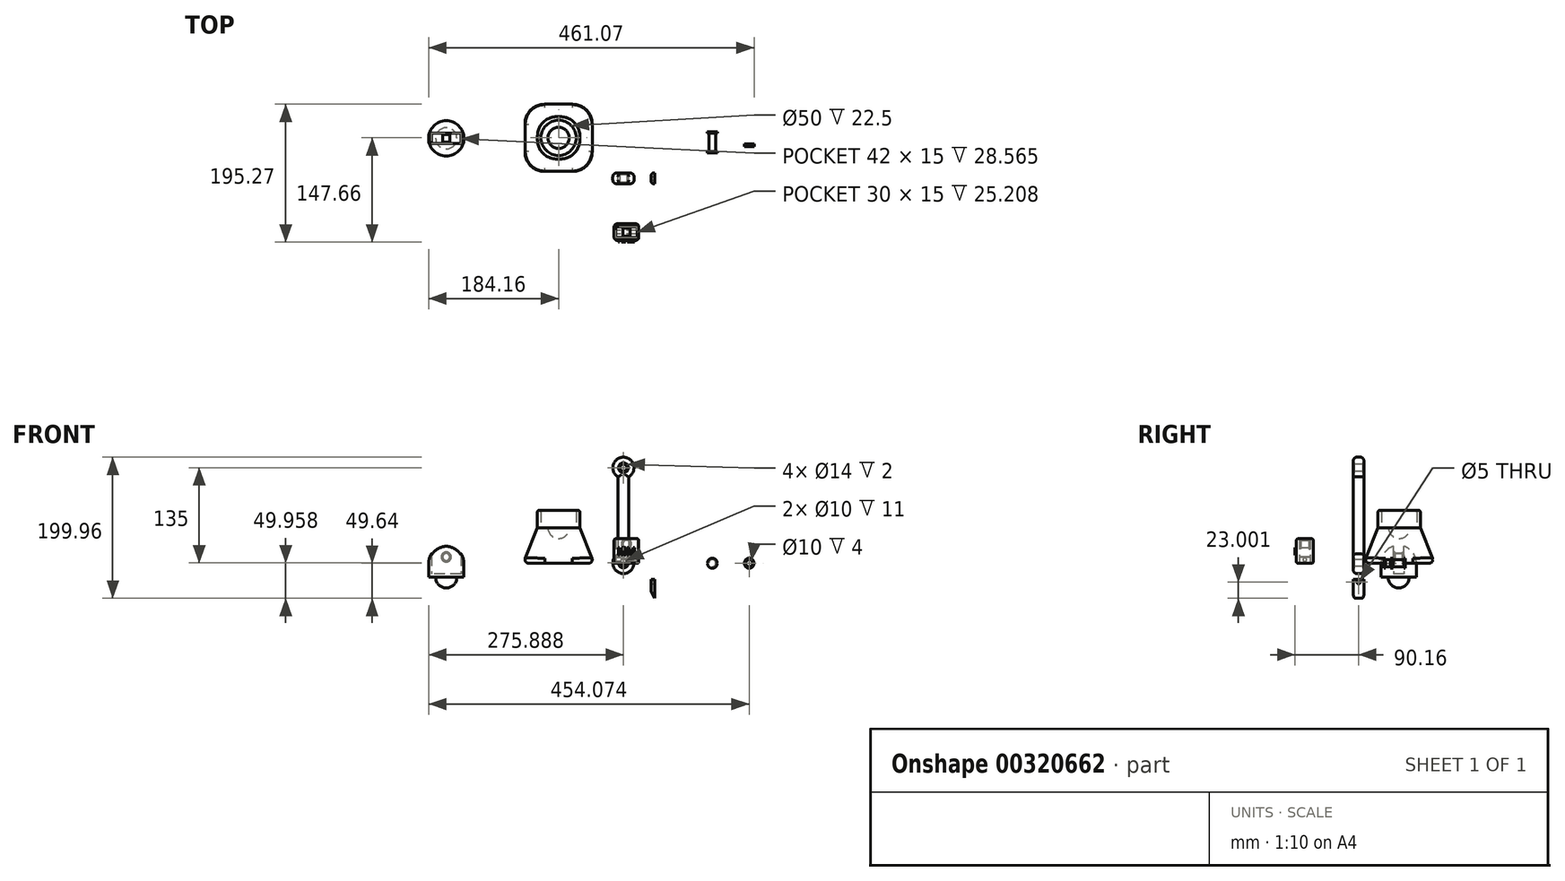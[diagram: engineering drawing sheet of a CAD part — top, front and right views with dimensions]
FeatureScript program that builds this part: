
annotation { "Feature Type Name" : "Feature", "Feature Type Description" : "" }
export const myFeature = defineFeature(function(context is Context, id is Id, definition is map)
    precondition{}
    {
        {
            var Q0;
            Q0=qCreatedBy(makeId("Top.planeOp"),FACE);
            var sketch = newSketch(context, id + "F0", { "sketchPlane" : qUnion([Q0])});
            skLineSegment(sketch, "E0.bottom", {"start": v(0, 0) * mm, "end": v(100, 0) * mm});
            skLineSegment(sketch, "E0.top", {"start": v(0, 100) * mm, "end": v(100, 100) * mm});
            skLineSegment(sketch, "E0.left", {"start": v(0, 0) * mm, "end": v(0, 100) * mm});
            skLineSegment(sketch, "E0.right", {"start": v(100, 0) * mm, "end": v(100, 100) * mm});
            skSolve(sketch);
        }
        {
            var Q0;
            Q0=makeQuery(id+"F0.imprint","IMPRINT",FACE,{"disambiguationData":[TD([[makeQuery(id+"F0.imprint","IMPRINT",EDGE,{"derivedFrom":sQuery(id+"F0.wireOp",EDGE,"E0.bottom")}),1.0]])]});
            cPlane(context, id + "F1", {"entities" : qUnion([Q0]), "cplaneType" : CPlaneType.OFFSET, "offset" : 50 * mm, "width" : 150 * mm, "height" : 150 * mm});
        }
        {
            var Q0;
            Q0=qCreatedBy(id+"F1.planeOp",FACE);
            var sketch = newSketch(context, id + "F2", { "sketchPlane" : qUnion([Q0])});
            skLineSegment(sketch, "E1.bottom", {"start": v(20, 80) * mm, "end": v(80, 80) * mm});
            skLineSegment(sketch, "E1.top", {"start": v(20, 20) * mm, "end": v(80, 20) * mm});
            skLineSegment(sketch, "E1.left", {"start": v(20, 80) * mm, "end": v(20, 20) * mm});
            skLineSegment(sketch, "E1.right", {"start": v(80, 80) * mm, "end": v(80, 20) * mm});
            skSolve(sketch);
        }
        {
            var Q0;
            Q0=makeQuery(id+"F0.imprint","IMPRINT",FACE,{"disambiguationData":[TD([[makeQuery(id+"F0.imprint","IMPRINT",EDGE,{"derivedFrom":sQuery(id+"F0.wireOp",EDGE,"E0.bottom")}),1.0]])]});
            var Q1;
            Q1=makeQuery(id+"F2.imprint","IMPRINT",FACE,{"disambiguationData":[TD([[makeQuery(id+"F2.imprint","IMPRINT",EDGE,{"derivedFrom":sQuery(id+"F2.wireOp",EDGE,"E1.bottom")}),-1.0]])]});
            loft(context, id + "F3", {"sheetProfilesArray" : [{ "sheetProfileEntities" : qUnion([Q0]) }, { "sheetProfileEntities" : qUnion([Q1]) }]});
        }
        {
            var Q0;
            Q0=makeQuery(id+"F3.opLoft","CAP_FACE",FACE,{"disambiguationData":[OSD([makeQuery(id+"F2.imprint","IMPRINT",FACE,{"disambiguationData":[TD([[makeQuery(id+"F2.imprint","IMPRINT",EDGE,{"derivedFrom":sQuery(id+"F2.wireOp",EDGE,"E1.bottom")}),-1.0]])]})])],"isStart":true});
            var sketch = newSketch(context, id + "F4", { "sketchPlane" : qUnion([Q0])});
            skLineSegment(sketch, "E2", {"start": v(50, 65) * mm, "end": v(50, 35) * mm});
            skArc(sketch, "E3", {"start": v(50, 35) * mm, "mid": v(65, 50) * mm, "end": v(50, 65) * mm});
            skPoint(sketch, "E4.orphan", {"position": v(50, 80) * mm});
            skPoint(sketch, "E5.orphan", {"position": v(50, 20) * mm});
            skSolve(sketch);
        }
        {
            var Q0;
            Q0=makeQuery(id+"F4.imprint","IMPRINT",FACE,{"disambiguationData":[TD([[makeQuery(id+"F4.imprint","IMPRINT",EDGE,{"derivedFrom":sQuery(id+"F4.wireOp",EDGE,"E2")}),1.0]])]});
            var Q1;
            Q1=sQuery(id+"F4.wireOp",EDGE,"E2");
            revolve(context, id + "F5", {"operationType" : NewBodyOperationType.REMOVE, "entities" : qUnion([Q0]), "axis" : qUnion([Q1]), "revolveType" : RevolveType.FULL, "oppositeDirection" : true});
        }
        {
            var Q0;
            Q0=makeQuery(id+"F3.opLoft","CAP_FACE",FACE,{"disambiguationData":[OSD([makeQuery(id+"F0.imprint","IMPRINT",FACE,{"disambiguationData":[TD([[makeQuery(id+"F0.imprint","IMPRINT",EDGE,{"derivedFrom":sQuery(id+"F0.wireOp",EDGE,"E0.bottom")}),1.0]])]})])],"isStart":true});
            fillet(context, id + "F6", {"entities" : qUnion([Q0]), "radius" : 5 * mm, "tangentPropagation" : true, "allowEdgeOverflow" : false});
        }
        {
            var Q0;
            Q0=makeQuery(id+"F3.opLoft","SWEPT_EDGE",EDGE,{"disambiguationData":[OSD([sQuery(id+"F0.wireOp",EDGE,"E0.bottom"),sQuery(id+"F0.wireOp",EDGE,"E0.right"),sQuery(id+"F2.wireOp",EDGE,"E1.top"),sQuery(id+"F2.wireOp",EDGE,"E1.right")])]});
            var Q1;
            Q1=makeQuery(id+"F3.opLoft","SWEPT_EDGE",EDGE,{"disambiguationData":[OSD([sQuery(id+"F0.wireOp",EDGE,"E0.top"),sQuery(id+"F0.wireOp",EDGE,"E0.right"),sQuery(id+"F2.wireOp",EDGE,"E1.bottom"),sQuery(id+"F2.wireOp",EDGE,"E1.right")])]});
            var Q2;
            Q2=makeQuery(id+"F3.opLoft","SWEPT_EDGE",EDGE,{"disambiguationData":[OSD([sQuery(id+"F0.wireOp",EDGE,"E0.top"),sQuery(id+"F0.wireOp",EDGE,"E0.left"),sQuery(id+"F2.wireOp",EDGE,"E1.bottom"),sQuery(id+"F2.wireOp",EDGE,"E1.left")])]});
            var Q3;
            Q3=makeQuery(id+"F3.opLoft","SWEPT_EDGE",EDGE,{"disambiguationData":[OSD([sQuery(id+"F0.wireOp",EDGE,"E0.bottom"),sQuery(id+"F0.wireOp",EDGE,"E0.left"),sQuery(id+"F2.wireOp",EDGE,"E1.top"),sQuery(id+"F2.wireOp",EDGE,"E1.left")])]});
            fillet(context, id + "F7", {"entities" : qUnion([Q0, Q1, Q2, Q3]), "radius" : 30 * mm, "tangentPropagation" : true, "allowEdgeOverflow" : false});
        }
        {
            var Q0;
            Q0=qCreatedBy(makeId("Top.planeOp"),FACE);
            var sketch = newSketch(context, id + "F8", { "sketchPlane" : qUnion([Q0])});
            skArc(sketch, "E6", {"start": v(184.89, 22.61) * mm, "mid": v(199.89, 37.61) * mm, "end": v(184.89, 52.61) * mm});
            skLineSegment(sketch, "E7", {"start": v(184.89, 22.61) * mm, "end": v(184.89, 52.61) * mm});
            skSolve(sketch);
        }
        {
            var Q0;
            Q0=qCreatedBy(makeId("Top.planeOp"),FACE);
            cPlane(context, id + "F9", {"entities" : qUnion([Q0]), "cplaneType" : CPlaneType.OFFSET, "offset" : 10 * mm, "width" : 150 * mm, "height" : 150 * mm});
        }
        {
            var Q0;
            Q0=qCreatedBy(id+"F9.planeOp",FACE);
            var sketch = newSketch(context, id + "F10", { "sketchPlane" : qUnion([Q0])});
            skLineSegment(sketch, "E8.bottom", {"start": v(177.39, 45.11) * mm, "end": v(192.39, 45.11) * mm});
            skLineSegment(sketch, "E8.top", {"start": v(177.39, 30.11) * mm, "end": v(192.39, 30.11) * mm});
            skLineSegment(sketch, "E8.left", {"start": v(177.39, 45.11) * mm, "end": v(177.39, 30.11) * mm});
            skLineSegment(sketch, "E8.right", {"start": v(192.39, 45.11) * mm, "end": v(192.39, 30.11) * mm});
            skSolve(sketch);
        }
        {
            var Q0;
            Q0=makeQuery(id+"F8.imprint","IMPRINT",FACE,{"disambiguationData":[TD([[makeQuery(id+"F8.imprint","IMPRINT",EDGE,{"derivedFrom":sQuery(id+"F8.wireOp",EDGE,"E6")}),1.0]])]});
            var Q1;
            Q1=sQuery(id+"F8.wireOp",EDGE,"E7");
            revolve(context, id + "F11", {"entities" : qUnion([Q0]), "axis" : qUnion([Q1]), "revolveType" : RevolveType.FULL});
        }
        {
            var Q0;
            Q0 = qSketchRegion(id + "F10", true);
            extrude(context, id + "F12", {"entities" : qUnion([Q0]), "operationType" : NewBodyOperationType.ADD, "depth" : 120 * mm});
        }
        {
            var Q0;
            Q0=makeQuery(id+"F12.boolean.opBoolean","INTERSECT",EDGE,{"derivedFrom":[makeQuery(id+"F11.opRevolve","SWEPT_FACE",FACE,{"disambiguationData":[OSD([sQuery(id+"F8.wireOp",EDGE,"E6")])]}),makeQuery(id+"F12.opExtrude","SWEPT_FACE",FACE,{"disambiguationData":[OSD([sQuery(id+"F10.wireOp",EDGE,"E8.right")])]})]});
            var Q1;
            Q1=makeQuery(id+"F12.boolean.opBoolean","INTERSECT",EDGE,{"derivedFrom":[makeQuery(id+"F11.opRevolve","SWEPT_FACE",FACE,{"disambiguationData":[OSD([sQuery(id+"F8.wireOp",EDGE,"E6")])]}),makeQuery(id+"F12.opExtrude","SWEPT_FACE",FACE,{"disambiguationData":[OSD([sQuery(id+"F10.wireOp",EDGE,"E8.top")])]})]});
            var Q2;
            Q2=makeQuery(id+"F12.boolean.opBoolean","INTERSECT",EDGE,{"derivedFrom":[makeQuery(id+"F11.opRevolve","SWEPT_FACE",FACE,{"disambiguationData":[OSD([sQuery(id+"F8.wireOp",EDGE,"E6")])]}),makeQuery(id+"F12.opExtrude","SWEPT_FACE",FACE,{"disambiguationData":[OSD([sQuery(id+"F10.wireOp",EDGE,"E8.bottom")])]})]});
            var Q3;
            Q3=makeQuery(id+"F12.boolean.opBoolean","INTERSECT",EDGE,{"derivedFrom":[makeQuery(id+"F11.opRevolve","SWEPT_FACE",FACE,{"disambiguationData":[OSD([sQuery(id+"F8.wireOp",EDGE,"E6")])]}),makeQuery(id+"F12.opExtrude","SWEPT_FACE",FACE,{"disambiguationData":[OSD([sQuery(id+"F10.wireOp",EDGE,"E8.left")])]})]});
            var Q4;
            Q4=makeQuery(id+"F12.opExtrude","SWEPT_EDGE",EDGE,{"disambiguationData":[OSD([sQuery(id+"F10.wireOp",EDGE,"E8.bottom"),sQuery(id+"F10.wireOp",EDGE,"E8.left")])]});
            var Q5;
            Q5=makeQuery(id+"F12.opExtrude","SWEPT_EDGE",EDGE,{"disambiguationData":[OSD([sQuery(id+"F10.wireOp",EDGE,"E8.bottom"),sQuery(id+"F10.wireOp",EDGE,"E8.right")])]});
            var Q6;
            Q6=makeQuery(id+"F12.opExtrude","SWEPT_EDGE",EDGE,{"disambiguationData":[OSD([sQuery(id+"F10.wireOp",EDGE,"E8.top"),sQuery(id+"F10.wireOp",EDGE,"E8.right")])]});
            var Q7;
            Q7=makeQuery(id+"F12.opExtrude","SWEPT_EDGE",EDGE,{"disambiguationData":[OSD([sQuery(id+"F10.wireOp",EDGE,"E8.top"),sQuery(id+"F10.wireOp",EDGE,"E8.left")])]});
            fillet(context, id + "F13", {"entities" : qUnion([Q0, Q1, Q2, Q3, Q4, Q5, Q6, Q7]), "radius" : 5 * mm, "tangentPropagation" : true, "allowEdgeOverflow" : false});
        }
        {
            var Q0;
            Q0=makeQuery(id+"F12.opExtrude","CAP_EDGE",EDGE,{"disambiguationData":[OSD([sQuery(id+"F10.wireOp",EDGE,"E8.right")])],"isStart":false});
            cPoint(context, id + "F14", {"entities" : qUnion([Q0]), "parameter" : 0.5});
        }
        {
            var Q0;
            Q0=makeQuery(id+"F12.opExtrude","CAP_EDGE",EDGE,{"disambiguationData":[OSD([sQuery(id+"F10.wireOp",EDGE,"E8.left")])],"isStart":false});
            cPoint(context, id + "F15", {"entities" : qUnion([Q0]), "parameter" : 0.5});
        }
        {
            var Q0;
            {var subQ0=makeQuery(id+"F12.opExtrude","SWEPT_FACE",FACE,{"disambiguationData":[OSD([sQuery(id+"F10.wireOp",EDGE,"E8.left")])]});Q0=makeQuery(id+"F13.opFillet","BLEND_EDGE",EDGE,{"blendedFrom":[makeQuery(id+"F12.boolean.opBoolean","INTERSECT",EDGE,{"derivedFrom":[makeQuery(id+"F11.opRevolve","SWEPT_FACE",FACE,{"disambiguationData":[OSD([sQuery(id+"F8.wireOp",EDGE,"E6")])]}),subQ0]}),subQ0],"blendedInto":[subQ0]});}
            cPoint(context, id + "F16", {"entities" : qUnion([Q0]), "parameter" : 0.5});
        }
        {
            var Q0;
            Q0 = qCreatedBy(id + "F14" ,VERTEX);
            var Q1;
            Q1 = qCreatedBy(id + "F15" ,VERTEX);
            var Q2;
            Q2 = qCreatedBy(id + "F16" ,VERTEX);
            cPlane(context, id + "F17", {"entities" : qUnion([Q0, Q1, Q2]), "cplaneType" : CPlaneType.THREE_POINT, "offset" : 25 * mm, "width" : 150 * mm, "height" : 150 * mm});
        }
        {
            var Q0;
            Q0=qCreatedBy(id+"F17.planeOp",FACE);
            var sketch = newSketch(context, id + "F18", { "sketchPlane" : qUnion([Q0])});
            skCircle(sketch, "E9", {"center": v(-184.89, 137.5) * mm, "radius": 15 * mm});
            skSolve(sketch);
        }
        {
            var Q0;
            Q0=makeQuery(id+"F18.imprint","IMPRINT",FACE,{"disambiguationData":[TD([[makeQuery(id+"F18.imprint","IMPRINT",EDGE,{"derivedFrom":sQuery(id+"F18.wireOp",EDGE,"E9")}),1.0]])]});
            extrude(context, id + "F19", {"entities" : qUnion([Q0]), "operationType" : NewBodyOperationType.ADD, "endBound" : BoundingType.SYMMETRIC, "depth" : 15 * mm});
        }
        {
            var Q0;
            Q0=makeQuery(id+"F19.opExtrude","CAP_EDGE",EDGE,{"disambiguationData":[OSD([sQuery(id+"F18.wireOp",EDGE,"E9")])],"isStart":true});
            var Q1;
            Q1=makeQuery(id+"F19.opExtrude","CAP_EDGE",EDGE,{"disambiguationData":[OSD([sQuery(id+"F18.wireOp",EDGE,"E9")])],"isStart":false});
            fillet(context, id + "F20", {"entities" : qUnion([Q0, Q1]), "radius" : 5 * mm, "tangentPropagation" : true, "allowEdgeOverflow" : false});
        }
        {
            var Q0;
            Q0=makeQuery(id+"F19.boolean.opBoolean","MERGE",FACE,{"derivedFrom":[makeQuery(id+"F12.opExtrude","SWEPT_FACE",FACE,{"disambiguationData":[OSD([sQuery(id+"F10.wireOp",EDGE,"E8.top")])]}),makeQuery(id+"F19.opExtrude","CAP_FACE",FACE,{"disambiguationData":[OSD([sQuery(id+"F18.wireOp",EDGE,"E9")])],"isStart":true})]});
            var sketch = newSketch(context, id + "F21", { "sketchPlane" : qUnion([Q0])});
            skCircle(sketch, "E10", {"center": v(184.89, 137.5) * mm, "radius": 5 * mm});
            skCircle(sketch, "E11", {"center": v(184.89, 137.5) * mm, "radius": 7 * mm});
            skSolve(sketch);
        }
        {
            var Q0;
            Q0=sQuery(id+"F21.wireOp",VERTEX,"E10.center");
            var Q1;
            Q1=makeQuery(id+"F11.opRevolve","SWEPT_BODY",BODY,{"disambiguationData":[OSD([sQuery(id+"F8.wireOp",EDGE,"E6"),sQuery(id+"F8.wireOp",EDGE,"E7")])]});
            hole(context, id + "F22", {"style" : HoleStyle.SIMPLE, "endStyle" : HoleEndStyle.THROUGH, "holeDiameter" : 10 * mm, "tappedDepth" : 12 * mm, "tapClearance" : 3, "locations" : qUnion([Q0]), "scope" : qUnion([Q1])});
        }
        {
            var Q0;
            Q0=makeQuery(id+"F19.boolean.opBoolean","MERGE",FACE,{"derivedFrom":[makeQuery(id+"F12.opExtrude","SWEPT_FACE",FACE,{"disambiguationData":[OSD([sQuery(id+"F10.wireOp",EDGE,"E8.bottom")])]}),makeQuery(id+"F19.opExtrude","CAP_FACE",FACE,{"disambiguationData":[OSD([sQuery(id+"F18.wireOp",EDGE,"E9")])],"isStart":false})]});
            var sketch = newSketch(context, id + "F23", { "sketchPlane" : qUnion([Q0])});
            skCircle(sketch, "E12", {"center": v(-184.89, 137.5) * mm, "radius": 7 * mm});
            skSolve(sketch);
        }
        {
            var Q0;
            Q0 = qSketchRegion(id + "F21", true);
            var Q1;
            Q1 = qSketchRegion(id + "F23", true);
            extrude(context, id + "F24", {"entities" : qUnion([Q0, Q1]), "operationType" : NewBodyOperationType.REMOVE, "oppositeDirection" : true, "depth" : 2 * mm, "hasSecondDirection" : true, "secondDirectionOppositeDirection" : false, "secondDirectionDepth" : 2 * mm});
        }
        {
            var Q0;
            Q0=qCreatedBy(makeId("Top.planeOp"),FACE);
            var sketch = newSketch(context, id + "F25", { "sketchPlane" : qUnion([Q0])});
            skLineSegment(sketch, "E13.bottom", {"start": v(267.71, 58.7) * mm, "end": v(272.71, 58.7) * mm});
            skLineSegment(sketch, "E13.top", {"start": v(267.71, 28.7) * mm, "end": v(272.71, 28.7) * mm});
            skLineSegment(sketch, "E13.left", {"start": v(267.71, 58.7) * mm, "end": v(267.71, 28.7) * mm});
            skLineSegment(sketch, "E13.right", {"start": v(272.71, 56.7) * mm, "end": v(272.71, 30.7) * mm});
            skLineSegment(sketch, "E14.bottom", {"start": v(272.71, 58.7) * mm, "end": v(274.71, 58.7) * mm});
            skLineSegment(sketch, "E14.top", {"start": v(272.71, 56.7) * mm, "end": v(274.71, 56.7) * mm});
            skLineSegment(sketch, "E14.right", {"start": v(274.71, 58.7) * mm, "end": v(274.71, 56.7) * mm});
            skLineSegment(sketch, "E15.bottom", {"start": v(272.71, 28.7) * mm, "end": v(274.71, 28.7) * mm});
            skLineSegment(sketch, "E15.top", {"start": v(272.71, 30.7) * mm, "end": v(274.71, 30.7) * mm});
            skLineSegment(sketch, "E15.right", {"start": v(274.71, 28.7) * mm, "end": v(274.71, 30.7) * mm});
            skSolve(sketch);
        }
        {
            var Q0;
            Q0=makeQuery(id+"F25.imprint","IMPRINT",FACE,{"disambiguationData":[TD([[makeQuery(id+"F25.imprint","IMPRINT",EDGE,{"derivedFrom":sQuery(id+"F25.wireOp",EDGE,"E13.bottom")}),-1.0]])]});
            var Q1;
            Q1=sQuery(id+"F25.wireOp",EDGE,"E13.left");
            revolve(context, id + "F26", {"entities" : qUnion([Q0]), "axis" : qUnion([Q1]), "revolveType" : RevolveType.FULL});
        }
        {
            var Q0;
            Q0=qCreatedBy(id+"F17.planeOp",FACE);
            var sketch = newSketch(context, id + "F27", { "sketchPlane" : qUnion([Q0])});
            skCircle(sketch, "E16", {"center": v(-319.91, 0) * mm, "radius": 7 * mm});
            skCircle(sketch, "E17", {"center": v(-319.91, 0) * mm, "radius": 5 * mm});
            skSolve(sketch);
        }
        {
            var Q0;
            Q0 = qSketchRegion(id + "F27", true);
            extrude(context, id + "F28", {"entities" : qUnion([Q0]), "depth" : 4 * mm});
        }
        {
            var Q0;
            Q0=qCreatedBy(makeId("Top.planeOp"),FACE);
            var sketch = newSketch(context, id + "F29", { "sketchPlane" : qUnion([Q0])});
            skArc(sketch, "E18", {"start": v(-109.16, 24.23) * mm, "mid": v(-84.16, 49.23) * mm, "end": v(-109.16, 74.23) * mm});
            skLineSegment(sketch, "E19", {"start": v(-109.16, 74.23) * mm, "end": v(-109.16, 24.23) * mm});
            skSolve(sketch);
        }
        {
            var Q0;
            Q0=makeQuery(id+"F29.imprint","IMPRINT",FACE,{"disambiguationData":[TD([[makeQuery(id+"F29.imprint","IMPRINT",EDGE,{"derivedFrom":sQuery(id+"F29.wireOp",EDGE,"E18")}),1.0]])]});
            var Q1;
            Q1=sQuery(id+"F29.wireOp",EDGE,"E19");
            revolve(context, id + "F30", {"entities" : qUnion([Q0]), "axis" : qUnion([Q1]), "revolveType" : RevolveType.ONE_DIRECTION, "angle" : 180 * degree});
        }
        {
            var Q0;
            Q0=qCreatedBy(makeId("Front.planeOp"),FACE);
            var sketch = newSketch(context, id + "F31", { "sketchPlane" : qUnion([Q0])});
            skLineSegment(sketch, "E20.left", {"start": v(134.23, 122.33) * mm, "end": v(134.23, 13.3) * mm});
            skLineSegment(sketch, "E20.right", {"start": v(149.23, 122.33) * mm, "end": v(149.23, 13.3) * mm});
            skArc(sketch, "E21", {"start": v(149.23, 122.33) * mm, "mid": v(141.73, 150.32) * mm, "end": v(134.23, 122.33) * mm});
            skArc(sketch, "E22", {"start": v(134.23, 13.3) * mm, "mid": v(141.73, -14.68) * mm, "end": v(149.23, 13.3) * mm});
            skSolve(sketch);
        }
        {
            var Q0;
            Q0=makeQuery(id+"F31.imprint","IMPRINT",FACE,{"disambiguationData":[TD([[makeQuery(id+"F31.imprint","IMPRINT",EDGE,{"derivedFrom":sQuery(id+"F31.wireOp",EDGE,"E20.left")}),1.0]])]});
            extrude(context, id + "F32", {"entities" : qUnion([Q0]), "depth" : 15 * mm});
        }
        {
            var Q0;
            Q0=makeQuery(id+"F32.opExtrude","CAP_FACE",FACE,{"disambiguationData":[OSD([sQuery(id+"F31.wireOp",EDGE,"E20.left"),sQuery(id+"F31.wireOp",EDGE,"E20.right"),sQuery(id+"F31.wireOp",EDGE,"E21"),sQuery(id+"F31.wireOp",EDGE,"E22")])],"isStart":false});
            var Q1;
            Q1=makeQuery(id+"F32.opExtrude","CAP_FACE",FACE,{"disambiguationData":[OSD([sQuery(id+"F31.wireOp",EDGE,"E20.left"),sQuery(id+"F31.wireOp",EDGE,"E20.right"),sQuery(id+"F31.wireOp",EDGE,"E21"),sQuery(id+"F31.wireOp",EDGE,"E22")])],"isStart":true});
            fillet(context, id + "F33", {"entities" : qUnion([Q0, Q1]), "radius" : 5 * mm, "tangentPropagation" : true, "allowEdgeOverflow" : false});
        }
        {
            var Q0;
            Q0=makeQuery(id+"F32.opExtrude","CAP_FACE",FACE,{"disambiguationData":[OSD([sQuery(id+"F31.wireOp",EDGE,"E20.left"),sQuery(id+"F31.wireOp",EDGE,"E20.right"),sQuery(id+"F31.wireOp",EDGE,"E21"),sQuery(id+"F31.wireOp",EDGE,"E22")])],"isStart":false});
            var sketch = newSketch(context, id + "F34", { "sketchPlane" : qUnion([Q0])});
            skCircle(sketch, "E23", {"center": v(141.73, 135.32) * mm, "radius": 5 * mm});
            skCircle(sketch, "E24", {"center": v(141.73, 0.32) * mm, "radius": 5 * mm});
            skCircle(sketch, "E25", {"center": v(141.73, 135.32) * mm, "radius": 7 * mm});
            skCircle(sketch, "E26", {"center": v(141.73, 0.32) * mm, "radius": 7 * mm});
            skSolve(sketch);
        }
        {
            var Q0;
            Q0=makeQuery(id+"F34.imprint","IMPRINT",FACE,{"disambiguationData":[TD([[makeQuery(id+"F34.imprint","IMPRINT",EDGE,{"derivedFrom":sQuery(id+"F34.wireOp",EDGE,"E23")}),1.0]])]});
            var Q1;
            Q1=makeQuery(id+"F34.imprint","IMPRINT",FACE,{"disambiguationData":[TD([[makeQuery(id+"F34.imprint","IMPRINT",EDGE,{"derivedFrom":sQuery(id+"F34.wireOp",EDGE,"E24")}),1.0]])]});
            extrude(context, id + "F35", {"entities" : qUnion([Q0, Q1]), "operationType" : NewBodyOperationType.REMOVE, "endBound" : BoundingType.THROUGH_ALL, "oppositeDirection" : true, "depth" : 25 * mm});
        }
        {
            var Q0;
            Q0 = qSketchRegion(id + "F34", true);
            extrude(context, id + "F36", {"entities" : qUnion([Q0]), "operationType" : NewBodyOperationType.REMOVE, "oppositeDirection" : true, "depth" : 2 * mm});
        }
        {
            var Q0;
            Q0=makeQuery(id+"F32.opExtrude","CAP_FACE",FACE,{"disambiguationData":[OSD([sQuery(id+"F31.wireOp",EDGE,"E20.left"),sQuery(id+"F31.wireOp",EDGE,"E20.right"),sQuery(id+"F31.wireOp",EDGE,"E21"),sQuery(id+"F31.wireOp",EDGE,"E22")])],"isStart":true});
            var sketch = newSketch(context, id + "F37", { "sketchPlane" : qUnion([Q0])});
            skCircle(sketch, "E27", {"center": v(-141.73, 135.32) * mm, "radius": 7 * mm});
            skCircle(sketch, "E28", {"center": v(-141.73, 0.32) * mm, "radius": 7 * mm});
            skSolve(sketch);
        }
        {
            var Q0;
            Q0 = qSketchRegion(id + "F37", true);
            extrude(context, id + "F38", {"entities" : qUnion([Q0]), "operationType" : NewBodyOperationType.REMOVE, "oppositeDirection" : true, "depth" : 2 * mm});
        }
        {
            var Q0;
            Q0=makeQuery(id+"F30.opRevolve","CAP_FACE",FACE,{"disambiguationData":[OSD([sQuery(id+"F29.wireOp",EDGE,"E18"),sQuery(id+"F29.wireOp",EDGE,"E19")])],"isStart":true});
            var sketch = newSketch(context, id + "F39", { "sketchPlane" : qUnion([Q0])});
            skLineSegment(sketch, "E29.bottom", {"start": v(-88.16, -56.73) * mm, "end": v(-130.16, -56.73) * mm});
            skLineSegment(sketch, "E29.top", {"start": v(-88.16, -41.73) * mm, "end": v(-130.16, -41.73) * mm});
            skLineSegment(sketch, "E29.left", {"start": v(-88.16, -56.73) * mm, "end": v(-88.16, -41.73) * mm});
            skLineSegment(sketch, "E29.right", {"start": v(-130.16, -56.73) * mm, "end": v(-130.16, -41.73) * mm});
            skSolve(sketch);
        }
        {
            var Q0;
            Q0=makeQuery(id+"F39.imprint","IMPRINT",FACE,{"disambiguationData":[TD([[makeQuery(id+"F39.imprint","IMPRINT",EDGE,{"derivedFrom":sQuery(id+"F39.wireOp",EDGE,"E29.bottom")}),1.0]])]});
            var Q1;
            Q1=makeQuery(id+"F39.imprint","IMPRINT",FACE,{"disambiguationData":[TD([[makeQuery(id+"F39.imprint","IMPRINT",EDGE,{"derivedFrom":sQuery(id+"F39.wireOp",EDGE,"E29.bottom")}),-1.0]])]});
            extrude(context, id + "F40", {"entities" : qUnion([Q0, Q1]), "operationType" : NewBodyOperationType.ADD, "depth" : 20 * mm});
        }
        {
            var Q0;
            Q0=makeQuery(id+"F40.opExtrude","CAP_FACE",FACE,{"disambiguationData":[OSD([sQuery(id+"F29.wireOp",EDGE,"E18")])],"isStart":false});
            var sketch = newSketch(context, id + "F41", { "sketchPlane" : qUnion([Q0])});
            skArc(sketch, "E30", {"start": v(-109.16, -34.23) * mm, "mid": v(-124.16, -49.23) * mm, "end": v(-109.16, -64.23) * mm});
            skLineSegment(sketch, "E31", {"start": v(-109.16, -64.23) * mm, "end": v(-109.16, -34.23) * mm});
            skSolve(sketch);
        }
        {
            var Q0;
            Q0=makeQuery(id+"F41.imprint","IMPRINT",FACE,{"disambiguationData":[TD([[makeQuery(id+"F41.imprint","IMPRINT",EDGE,{"derivedFrom":sQuery(id+"F41.wireOp",EDGE,"E30")}),1.0]])]});
            var Q1;
            Q1=sQuery(id+"F41.wireOp",EDGE,"E31");
            revolve(context, id + "F42", {"operationType" : NewBodyOperationType.ADD, "entities" : qUnion([Q0]), "axis" : qUnion([Q1]), "revolveType" : RevolveType.FULL});
        }
        {
            var Q0;
            Q0 = qSketchRegion(id + "F39", true);
            extrude(context, id + "F43", {"entities" : qUnion([Q0]), "operationType" : NewBodyOperationType.REMOVE, "endBound" : BoundingType.THROUGH_ALL, "oppositeDirection" : true, "depth" : 25 * mm, "hasSecondDirection" : true, "secondDirectionOppositeDirection" : false, "secondDirectionDepth" : 15 * mm});
        }
        {
            var Q0;
            Q0=makeQuery(id+"F43.boolean.opBoolean","COPY",FACE,{"derivedFrom":makeQuery(id+"F43.opExtrude","SWEPT_FACE",FACE,{"disambiguationData":[OSD([sQuery(id+"F39.wireOp",EDGE,"E29.top")])]})});
            var sketch = newSketch(context, id + "F44", { "sketchPlane" : qUnion([Q0])});
            skCircle(sketch, "E32", {"center": v(109.16, 8.85) * mm, "radius": 7 * mm});
            skPoint(sketch, "E32.centerSnap0", {"position": v(109.16, 23.85) * mm});
            skPoint(sketch, "E32.centerSnap1", {"position": v(130.16, -1.85) * mm});
            skSolve(sketch);
        }
        {
            var Q0;
            Q0=makeQuery(id+"F44.imprint","IMPRINT",FACE,{"disambiguationData":[TD([[makeQuery(id+"F44.imprint","IMPRINT",EDGE,{"derivedFrom":sQuery(id+"F44.wireOp",EDGE,"E32")}),1.0]])]});
            extrude(context, id + "F45", {"entities" : qUnion([Q0]), "operationType" : NewBodyOperationType.ADD, "depth" : 2 * mm});
        }
        {
            var Q0;
            Q0=makeQuery(id+"F45.opExtrude","CAP_FACE",FACE,{"disambiguationData":[OSD([sQuery(id+"F44.wireOp",EDGE,"E32")])],"isStart":false});
            var sketch = newSketch(context, id + "F46", { "sketchPlane" : qUnion([Q0])});
            skCircle(sketch, "E33", {"center": v(109.16, 8.85) * mm, "radius": 5 * mm});
            skSolve(sketch);
        }
        {
            var Q0;
            Q0=makeQuery(id+"F46.imprint","IMPRINT",FACE,{"disambiguationData":[TD([[makeQuery(id+"F46.imprint","IMPRINT",EDGE,{"derivedFrom":sQuery(id+"F46.wireOp",EDGE,"E33")}),1.0]])]});
            extrude(context, id + "F47", {"entities" : qUnion([Q0]), "operationType" : NewBodyOperationType.ADD, "endBound" : BoundingType.UP_TO_NEXT, "depth" : 25 * mm});
        }
        {
            var Q0;
            Q0=qCreatedBy(makeId("Top.planeOp"),FACE);
            var sketch = newSketch(context, id + "F48", { "sketchPlane" : qUnion([Q0])});
            skLineSegment(sketch, "E34.bottom", {"start": v(203.21, -84.7) * mm, "end": v(208.21, -84.7) * mm});
            skLineSegment(sketch, "E34.top", {"start": v(203.21, -99.7) * mm, "end": v(208.21, -99.7) * mm});
            skLineSegment(sketch, "E34.left", {"start": v(198.21, -89.7) * mm, "end": v(198.21, -94.7) * mm});
            skLineSegment(sketch, "E34.right", {"start": v(213.21, -89.7) * mm, "end": v(213.21, -94.7) * mm});
            skPoint(sketch, "E35.visualSharp", {"position": v(198.21, -84.7) * mm});
            skArc(sketch, "E35.filletArc", {"start": v(203.21, -84.7) * mm, "mid": v(199.68, -86.16) * mm, "end": v(198.21, -89.7) * mm});
            skPoint(sketch, "E36.visualSharp", {"position": v(213.21, -84.7) * mm});
            skArc(sketch, "E36.filletArc", {"start": v(213.21, -89.7) * mm, "mid": v(211.75, -86.16) * mm, "end": v(208.21, -84.7) * mm});
            skPoint(sketch, "E37.visualSharp", {"position": v(213.21, -99.7) * mm});
            skArc(sketch, "E37.filletArc", {"start": v(208.21, -99.7) * mm, "mid": v(211.75, -98.23) * mm, "end": v(213.21, -94.7) * mm});
            skPoint(sketch, "E38.visualSharp", {"position": v(198.21, -99.7) * mm});
            skArc(sketch, "E38.filletArc", {"start": v(198.21, -94.7) * mm, "mid": v(199.68, -98.23) * mm, "end": v(203.21, -99.7) * mm});
            skLineSegment(sketch, "E39.bottom", {"start": v(192.71, -74.2) * mm, "end": v(218.71, -74.2) * mm});
            skLineSegment(sketch, "E39.top", {"start": v(192.71, -110.2) * mm, "end": v(218.71, -110.2) * mm});
            skLineSegment(sketch, "E39.left", {"start": v(187.71, -79.2) * mm, "end": v(187.71, -105.2) * mm});
            skLineSegment(sketch, "E39.right", {"start": v(223.71, -79.2) * mm, "end": v(223.71, -105.2) * mm});
            skPoint(sketch, "E40.visualSharp", {"position": v(187.71, -74.2) * mm});
            skArc(sketch, "E40.filletArc", {"start": v(192.71, -74.2) * mm, "mid": v(189.18, -75.66) * mm, "end": v(187.71, -79.2) * mm});
            skPoint(sketch, "E41.visualSharp", {"position": v(223.71, -74.2) * mm});
            skArc(sketch, "E41.filletArc", {"start": v(223.71, -79.2) * mm, "mid": v(222.25, -75.66) * mm, "end": v(218.71, -74.2) * mm});
            skPoint(sketch, "E42.visualSharp", {"position": v(223.71, -110.2) * mm});
            skArc(sketch, "E42.filletArc", {"start": v(218.71, -110.2) * mm, "mid": v(222.25, -108.73) * mm, "end": v(223.71, -105.2) * mm});
            skPoint(sketch, "E43.visualSharp", {"position": v(187.71, -110.2) * mm});
            skArc(sketch, "E43.filletArc", {"start": v(187.71, -105.2) * mm, "mid": v(189.18, -108.73) * mm, "end": v(192.71, -110.2) * mm});
            skSolve(sketch);
        }
        {
            var Q0;
            Q0=makeQuery(id+"F48.imprint","IMPRINT",FACE,{"disambiguationData":[TD([[makeQuery(id+"F48.imprint","IMPRINT",EDGE,{"derivedFrom":sQuery(id+"F48.wireOp",EDGE,"E34.bottom")}),1.0]])]});
            extrude(context, id + "F49", {"entities" : qUnion([Q0]), "depth" : 20 * mm});
        }
        {
            var Q0;
            Q0=makeQuery(id+"F49.opExtrude","CAP_EDGE",EDGE,{"disambiguationData":[OSD([sQuery(id+"F48.wireOp",EDGE,"E39.left")])],"isStart":false});
            fillet(context, id + "F50", {"entities" : qUnion([Q0]), "radius" : 10 * mm, "tangentPropagation" : true, "allowEdgeOverflow" : false});
        }
        {
            var Q0;
            Q0=makeQuery(id+"F49.opExtrude","CAP_EDGE",EDGE,{"disambiguationData":[OSD([sQuery(id+"F48.wireOp",EDGE,"E34.top")])],"isStart":true});
            var Q1;
            Q1=makeQuery(id+"F49.opExtrude","CAP_EDGE",EDGE,{"disambiguationData":[OSD([sQuery(id+"F48.wireOp",EDGE,"E37.filletArc")])],"isStart":true});
            fillet(context, id + "F51", {"entities" : qUnion([Q0, Q1]), "radius" : 5 * mm, "tangentPropagation" : true, "allowEdgeOverflow" : false});
        }
        {
            var Q0;
            Q0=makeQuery(id+"F11.opRevolve","SWEPT_BODY",BODY,{"disambiguationData":[OSD([sQuery(id+"F8.wireOp",EDGE,"E6"),sQuery(id+"F8.wireOp",EDGE,"E7")])]});
            deleteBodies(context, id + "F52", {"entities" : qUnion([Q0])});
        }
        {
            var Q0;
            Q0=makeQuery(id+"F49.opExtrude","SWEPT_BODY",BODY,{"disambiguationData":[OSD([sQuery(id+"F48.wireOp",EDGE,"E34.bottom"),sQuery(id+"F48.wireOp",EDGE,"E34.top"),sQuery(id+"F48.wireOp",EDGE,"E34.left"),sQuery(id+"F48.wireOp",EDGE,"E34.right"),sQuery(id+"F48.wireOp",EDGE,"E35.filletArc"),sQuery(id+"F48.wireOp",EDGE,"E36.filletArc"),sQuery(id+"F48.wireOp",EDGE,"E37.filletArc"),sQuery(id+"F48.wireOp",EDGE,"E38.filletArc"),sQuery(id+"F48.wireOp",EDGE,"E39.bottom"),sQuery(id+"F48.wireOp",EDGE,"E39.top"),sQuery(id+"F48.wireOp",EDGE,"E39.left"),sQuery(id+"F48.wireOp",EDGE,"E39.right"),sQuery(id+"F48.wireOp",EDGE,"E40.filletArc"),sQuery(id+"F48.wireOp",EDGE,"E41.filletArc"),sQuery(id+"F48.wireOp",EDGE,"E42.filletArc"),sQuery(id+"F48.wireOp",EDGE,"E43.filletArc")])]});
            deleteBodies(context, id + "F53", {"entities" : qUnion([Q0])});
        }
        {
            var Q0;
            Q0=makeQuery(id+"F43.boolean.opBoolean","COPY",FACE,{"derivedFrom":makeQuery(id+"F43.opExtrude","SWEPT_FACE",FACE,{"disambiguationData":[OSD([sQuery(id+"F39.wireOp",EDGE,"E29.bottom")])]})});
            var sketch = newSketch(context, id + "F54", { "sketchPlane" : qUnion([Q0])});
            skCircle(sketch, "E44", {"center": v(-109.16, 8.85) * mm, "radius": 7 * mm});
            skSolve(sketch);
        }
        {
            var Q0;
            Q0=makeQuery(id+"F54.imprint","IMPRINT",FACE,{"disambiguationData":[TD([[makeQuery(id+"F54.imprint","IMPRINT",EDGE,{"derivedFrom":sQuery(id+"F54.wireOp",EDGE,"E44")}),1.0]])]});
            extrude(context, id + "F55", {"entities" : qUnion([Q0]), "operationType" : NewBodyOperationType.ADD, "depth" : 2 * mm});
        }
        {
            var Q0;
            Q0=qCreatedBy(makeId("Top.planeOp"),FACE);
            var sketch = newSketch(context, id + "F56", { "sketchPlane" : qUnion([Q0])});
            skLineSegment(sketch, "E45.bottom", {"start": v(133.56, -71.66) * mm, "end": v(158.56, -71.66) * mm});
            skLineSegment(sketch, "E45.top", {"start": v(133.56, -95.66) * mm, "end": v(158.56, -95.66) * mm});
            skLineSegment(sketch, "E45.left", {"start": v(128.56, -76.66) * mm, "end": v(128.56, -90.66) * mm});
            skLineSegment(sketch, "E45.right", {"start": v(163.56, -76.66) * mm, "end": v(163.56, -90.66) * mm});
            skPoint(sketch, "E46.visualSharp", {"position": v(163.56, -71.66) * mm});
            skArc(sketch, "E46.filletArc", {"start": v(163.56, -76.66) * mm, "mid": v(162.1, -73.13) * mm, "end": v(158.56, -71.66) * mm});
            skPoint(sketch, "E47.visualSharp", {"position": v(163.56, -95.66) * mm});
            skArc(sketch, "E47.filletArc", {"start": v(158.56, -95.66) * mm, "mid": v(162.1, -94.2) * mm, "end": v(163.56, -90.66) * mm});
            skPoint(sketch, "E48.visualSharp", {"position": v(128.56, -95.66) * mm});
            skArc(sketch, "E48.filletArc", {"start": v(128.56, -90.66) * mm, "mid": v(130.03, -94.2) * mm, "end": v(133.56, -95.66) * mm});
            skPoint(sketch, "E49.visualSharp", {"position": v(128.56, -71.66) * mm});
            skArc(sketch, "E49.filletArc", {"start": v(133.56, -71.66) * mm, "mid": v(130.03, -73.13) * mm, "end": v(128.56, -76.66) * mm});
            skPoint(sketch, "E50.firstSnap0", {"position": v(146.06, -71.66) * mm});
            skLineSegment(sketch, "E50.bottom", {"start": v(131.06, -76.16) * mm, "end": v(161.06, -76.16) * mm});
            skLineSegment(sketch, "E50.top", {"start": v(131.06, -91.16) * mm, "end": v(161.06, -91.16) * mm});
            skLineSegment(sketch, "E50.left", {"start": v(131.06, -76.16) * mm, "end": v(131.06, -91.16) * mm});
            skLineSegment(sketch, "E50.right", {"start": v(161.06, -76.16) * mm, "end": v(161.06, -91.16) * mm});
            skSolve(sketch);
        }
        {
            var Q0;
            Q0=makeQuery(id+"F56.imprint","IMPRINT",FACE,{"disambiguationData":[TD([[makeQuery(id+"F56.imprint","IMPRINT",EDGE,{"derivedFrom":sQuery(id+"F56.wireOp",EDGE,"E45.bottom")}),-1.0]])]});
            extrude(context, id + "F57", {"entities" : qUnion([Q0]), "depth" : 35 * mm});
        }
        {
            var Q0;
            Q0=makeQuery(id+"F57.opExtrude","SWEPT_FACE",FACE,{"disambiguationData":[OSD([sQuery(id+"F56.wireOp",EDGE,"E50.bottom")])]});
            var sketch = newSketch(context, id + "F58", { "sketchPlane" : qUnion([Q0])});
            skCircle(sketch, "E51", {"center": v(146.06, 27.5) * mm, "radius": 5 * mm});
            skCircle(sketch, "E52", {"center": v(146.06, 27.5) * mm, "radius": 7 * mm});
            skSolve(sketch);
        }
        {
            var Q0;
            Q0=makeQuery(id+"F58.imprint","IMPRINT",FACE,{"disambiguationData":[TD([[makeQuery(id+"F58.imprint","IMPRINT",EDGE,{"derivedFrom":sQuery(id+"F58.wireOp",EDGE,"E51")}),1.0]])]});
            extrude(context, id + "F59", {"entities" : qUnion([Q0]), "operationType" : NewBodyOperationType.ADD, "endBound" : BoundingType.UP_TO_NEXT, "depth" : 25 * mm});
        }
        {
            var Q0;
            Q0=makeQuery(id+"F58.imprint","IMPRINT",FACE,{"disambiguationData":[TD([[makeQuery(id+"F58.imprint","IMPRINT",EDGE,{"derivedFrom":sQuery(id+"F58.wireOp",EDGE,"E51")}),-1.0]])]});
            extrude(context, id + "F60", {"entities" : qUnion([Q0]), "operationType" : NewBodyOperationType.ADD, "depth" : 2 * mm});
        }
        {
            var Q0;
            Q0=makeQuery(id+"F57.opExtrude","SWEPT_FACE",FACE,{"disambiguationData":[OSD([sQuery(id+"F56.wireOp",EDGE,"E50.top")])]});
            var sketch = newSketch(context, id + "F61", { "sketchPlane" : qUnion([Q0])});
            skCircle(sketch, "E53", {"center": v(-146.06, 27.5) * mm, "radius": 7 * mm});
            skSolve(sketch);
        }
        {
            var Q0;
            Q0=makeQuery(id+"F61.imprint","IMPRINT",FACE,{"disambiguationData":[TD([[makeQuery(id+"F61.imprint","IMPRINT",EDGE,{"derivedFrom":sQuery(id+"F61.wireOp",EDGE,"E53")}),1.0]])]});
            extrude(context, id + "F62", {"entities" : qUnion([Q0]), "operationType" : NewBodyOperationType.ADD, "depth" : 2 * mm});
        }
        {
            var Q0;
            Q0=qCreatedBy(makeId("Front.planeOp"),FACE);
            var sketch = newSketch(context, id + "F63", { "sketchPlane" : qUnion([Q0])});
            skLineSegment(sketch, "E54", {"start": v(181.27, -22.64) * mm, "end": v(181.27, -40.64) * mm});
            skLineSegment(sketch, "E55", {"start": v(181.27, -40.64) * mm, "end": v(186.27, -49.64) * mm});
            skLineSegment(sketch, "E56", {"start": v(186.27, -49.64) * mm, "end": v(186.27, -22.64) * mm});
            skLineSegment(sketch, "E57", {"start": v(186.27, -22.64) * mm, "end": v(181.27, -22.64) * mm});
            skSolve(sketch);
        }
        {
            var Q0;
            Q0=makeQuery(id+"F63.imprint","IMPRINT",FACE,{"disambiguationData":[TD([[makeQuery(id+"F63.imprint","IMPRINT",EDGE,{"derivedFrom":sQuery(id+"F63.wireOp",EDGE,"E54")}),1.0]])]});
            extrude(context, id + "F64", {"entities" : qUnion([Q0]), "depth" : 15 * mm});
        }
        {
            var Q0;
            Q0=makeQuery(id+"F57.opExtrude","SWEPT_FACE",FACE,{"disambiguationData":[OSD([sQuery(id+"F56.wireOp",EDGE,"E50.left")])]});
            var sketch = newSketch(context, id + "F65", { "sketchPlane" : qUnion([Q0])});
            skCircle(sketch, "E58", {"center": v(-83.66, 5) * mm, "radius": 2.5 * mm});
            skPoint(sketch, "E58.centerSnap0", {"position": v(-83.66, 0) * mm});
            skLineSegment(sketch, "E59.bottom", {"start": v(-91.16, 9.75) * mm, "end": v(-76.16, 9.75) * mm});
            skLineSegment(sketch, "E59.top", {"start": v(-91.16, 9) * mm, "end": v(-76.16, 9) * mm});
            skLineSegment(sketch, "E59.left", {"start": v(-91.16, 9.75) * mm, "end": v(-91.16, 9) * mm});
            skLineSegment(sketch, "E59.right", {"start": v(-76.16, 9.75) * mm, "end": v(-76.16, 9) * mm});
            skSolve(sketch);
        }
        {
            var Q0;
            Q0=makeQuery(id+"F65.imprint","IMPRINT",FACE,{"disambiguationData":[TD([[makeQuery(id+"F65.imprint","IMPRINT",EDGE,{"derivedFrom":sQuery(id+"F65.wireOp",EDGE,"E58")}),1.0]])]});
            var Q1;
            Q1=makeQuery(id+"F65.imprint","IMPRINT",FACE,{"disambiguationData":[TD([[makeQuery(id+"F65.imprint","IMPRINT",EDGE,{"derivedFrom":sQuery(id+"F65.wireOp",EDGE,"E59.bottom")}),-1.0]])]});
            extrude(context, id + "F66", {"entities" : qUnion([Q0, Q1]), "operationType" : NewBodyOperationType.ADD, "endBound" : BoundingType.UP_TO_NEXT, "depth" : 25 * mm});
        }
        {
            var Q0;
            Q0=makeQuery(id+"F64.opExtrude","SWEPT_FACE",FACE,{"disambiguationData":[OSD([sQuery(id+"F63.wireOp",EDGE,"E56")])]});
            var sketch = newSketch(context, id + "F67", { "sketchPlane" : qUnion([Q0])});
            skCircle(sketch, "E60", {"center": v(-7.5, -26.64) * mm, "radius": 2.5 * mm});
            skPoint(sketch, "E60.centerSnap0", {"position": v(-7.5, -22.64) * mm});
            skSolve(sketch);
        }
        {
            var Q0;
            Q0=makeQuery(id+"F67.imprint","IMPRINT",FACE,{"disambiguationData":[TD([[makeQuery(id+"F67.imprint","IMPRINT",EDGE,{"derivedFrom":sQuery(id+"F67.wireOp",EDGE,"E60")}),1.0]])]});
            extrude(context, id + "F68", {"entities" : qUnion([Q0]), "operationType" : NewBodyOperationType.REMOVE, "endBound" : BoundingType.UP_TO_NEXT, "oppositeDirection" : true, "depth" : 25 * mm});
        }
        {
            var Q0;
            Q0=makeQuery(id+"F57.opExtrude","CAP_EDGE",EDGE,{"disambiguationData":[OSD([sQuery(id+"F56.wireOp",EDGE,"E45.top")])],"isStart":true});
            var Q1;
            Q1=makeQuery(id+"F57.opExtrude","CAP_EDGE",EDGE,{"disambiguationData":[OSD([sQuery(id+"F56.wireOp",EDGE,"E45.right")])],"isStart":true});
            var Q2;
            Q2=makeQuery(id+"F57.opExtrude","CAP_EDGE",EDGE,{"disambiguationData":[OSD([sQuery(id+"F56.wireOp",EDGE,"E47.filletArc")])],"isStart":true});
            var Q3;
            Q3=makeQuery(id+"F57.opExtrude","CAP_EDGE",EDGE,{"disambiguationData":[OSD([sQuery(id+"F56.wireOp",EDGE,"E45.bottom")])],"isStart":true});
            var Q4;
            Q4=makeQuery(id+"F57.opExtrude","CAP_EDGE",EDGE,{"disambiguationData":[OSD([sQuery(id+"F56.wireOp",EDGE,"E49.filletArc")])],"isStart":true});
            var Q5;
            Q5=makeQuery(id+"F57.opExtrude","CAP_EDGE",EDGE,{"disambiguationData":[OSD([sQuery(id+"F56.wireOp",EDGE,"E45.left")])],"isStart":true});
            var Q6;
            Q6=makeQuery(id+"F57.opExtrude","CAP_EDGE",EDGE,{"disambiguationData":[OSD([sQuery(id+"F56.wireOp",EDGE,"E48.filletArc")])],"isStart":true});
            var Q7;
            Q7=makeQuery(id+"F57.opExtrude","CAP_EDGE",EDGE,{"disambiguationData":[OSD([sQuery(id+"F56.wireOp",EDGE,"E46.filletArc")])],"isStart":true});
            fillet(context, id + "F69", {"entities" : qUnion([Q0, Q1, Q2, Q3, Q4, Q5, Q6, Q7]), "radius" : 2 * mm, "tangentPropagation" : true, "allowEdgeOverflow" : false});
        }
        {
            var Q0;
            Q0=makeQuery(id+"F57.opExtrude","CAP_EDGE",EDGE,{"disambiguationData":[OSD([sQuery(id+"F56.wireOp",EDGE,"E45.top")])],"isStart":false});
            var Q1;
            Q1=makeQuery(id+"F57.opExtrude","CAP_EDGE",EDGE,{"disambiguationData":[OSD([sQuery(id+"F56.wireOp",EDGE,"E46.filletArc")])],"isStart":false});
            var Q2;
            Q2=makeQuery(id+"F57.opExtrude","CAP_EDGE",EDGE,{"disambiguationData":[OSD([sQuery(id+"F56.wireOp",EDGE,"E47.filletArc")])],"isStart":false});
            var Q3;
            Q3=makeQuery(id+"F57.opExtrude","CAP_EDGE",EDGE,{"disambiguationData":[OSD([sQuery(id+"F56.wireOp",EDGE,"E48.filletArc")])],"isStart":false});
            var Q4;
            Q4=makeQuery(id+"F57.opExtrude","CAP_EDGE",EDGE,{"disambiguationData":[OSD([sQuery(id+"F56.wireOp",EDGE,"E45.left")])],"isStart":false});
            var Q5;
            Q5=makeQuery(id+"F57.opExtrude","CAP_EDGE",EDGE,{"disambiguationData":[OSD([sQuery(id+"F56.wireOp",EDGE,"E45.bottom")])],"isStart":false});
            var Q6;
            Q6=makeQuery(id+"F57.opExtrude","CAP_EDGE",EDGE,{"disambiguationData":[OSD([sQuery(id+"F56.wireOp",EDGE,"E49.filletArc")])],"isStart":false});
            fillet(context, id + "F70", {"entities" : qUnion([Q0, Q1, Q2, Q3, Q4, Q5, Q6]), "radius" : 3 * mm, "tangentPropagation" : true, "allowEdgeOverflow" : false});
        }
        {
            var Q0;
            Q0=makeQuery(id+"F64.opExtrude","CAP_EDGE",EDGE,{"disambiguationData":[OSD([sQuery(id+"F63.wireOp",EDGE,"E55")])],"isStart":false});
            var Q1;
            Q1=makeQuery(id+"F64.opExtrude","CAP_EDGE",EDGE,{"disambiguationData":[OSD([sQuery(id+"F63.wireOp",EDGE,"E55")])],"isStart":true});
            var Q2;
            Q2=makeQuery(id+"F64.opExtrude","SWEPT_EDGE",EDGE,{"disambiguationData":[OSD([sQuery(id+"F63.wireOp",EDGE,"E54"),sQuery(id+"F63.wireOp",EDGE,"E55")])]});
            var Q3;
            Q3=makeQuery(id+"F64.opExtrude","CAP_EDGE",EDGE,{"disambiguationData":[OSD([sQuery(id+"F63.wireOp",EDGE,"E54")])],"isStart":false});
            var Q4;
            Q4=makeQuery(id+"F64.opExtrude","CAP_EDGE",EDGE,{"disambiguationData":[OSD([sQuery(id+"F63.wireOp",EDGE,"E54")])],"isStart":true});
            fillet(context, id + "F71", {"entities" : qUnion([Q0, Q1, Q2, Q3, Q4]), "radius" : 3 * mm, "tangentPropagation" : true, "allowEdgeOverflow" : false});
        }
        {
            var Q0;
            Q0=makeQuery(id+"F3.opLoft","CAP_FACE",FACE,{"disambiguationData":[OSD([makeQuery(id+"F2.imprint","IMPRINT",FACE,{"disambiguationData":[TD([[makeQuery(id+"F2.imprint","IMPRINT",EDGE,{"derivedFrom":sQuery(id+"F2.wireOp",EDGE,"E1.bottom")}),-1.0]])]})])],"isStart":true});
            var sketch = newSketch(context, id + "F72", { "sketchPlane" : qUnion([Q0])});
            skCircle(sketch, "E61", {"center": v(50, 50) * mm, "radius": 25 * mm});
            skSolve(sketch);
        }
        {
            var Q0;
            Q0=makeQuery(id+"F72.imprint","IMPRINT",FACE,{"disambiguationData":[TD([[makeQuery(id+"F72.imprint","IMPRINT",EDGE,{"derivedFrom":sQuery(id+"F72.wireOp",EDGE,"E61")}),-1.0]])]});
            extrude(context, id + "F73", {"entities" : qUnion([Q0]), "operationType" : NewBodyOperationType.ADD, "depth" : 25 * mm});
        }
        {
            var Q0;
            {var subQ0=sQuery(id+"F2.wireOp",EDGE,"E1.bottom");var subQ1=sQuery(id+"F2.wireOp",EDGE,"E1.top");var subQ2=sQuery(id+"F2.wireOp",EDGE,"E1.left");var subQ3=sQuery(id+"F2.wireOp",EDGE,"E1.right");Q0=makeQuery(id+"F73.opExtrude","CAP_FACE",FACE,{"disambiguationData":[OSD([sQuery(id+"F0.wireOp",EDGE,"E0.bottom"),sQuery(id+"F0.wireOp",EDGE,"E0.top"),sQuery(id+"F0.wireOp",EDGE,"E0.left"),sQuery(id+"F0.wireOp",EDGE,"E0.right"),subQ0,subQ1,subQ2,subQ3,makeQuery(id+"F2.imprint","IMPRINT",FACE,{"disambiguationData":[TD([[makeQuery(id+"F2.imprint","IMPRINT",EDGE,{"derivedFrom":subQ0}),-1.0]])]}),sQuery(id+"F72.wireOp",EDGE,"E61")])],"isStart":false});}
            fillet(context, id + "F74", {"entities" : qUnion([Q0]), "radius" : 2.5 * mm, "tangentPropagation" : true, "allowEdgeOverflow" : false});
        }
        {
            var Q0;
            Q0=makeQuery(id+"F57.opExtrude","SWEPT_FACE",FACE,{"disambiguationData":[OSD([sQuery(id+"F56.wireOp",EDGE,"E45.top")])]});
            var sketch = newSketch(context, id + "F75", { "sketchPlane" : qUnion([Q0])});
            skText(sketch, "E62", { "text": "IEM\n\n", "fontName": "OpenSans-Regular.ttf"});
            const initialGuessF75  = {"E62": [0.13356, 0.01172, 1, 0, 0.01056]};
            skSetInitialGuess(sketch, initialGuessF75);
            skSolve(sketch);
        }
        {
            var Q0;
            Q0 = qSketchRegion(id + "F75", true);
            extrude(context, id + "F76", {"entities" : qUnion([Q0]), "operationType" : NewBodyOperationType.ADD, "depth" : 2 * mm});
        }
    });
